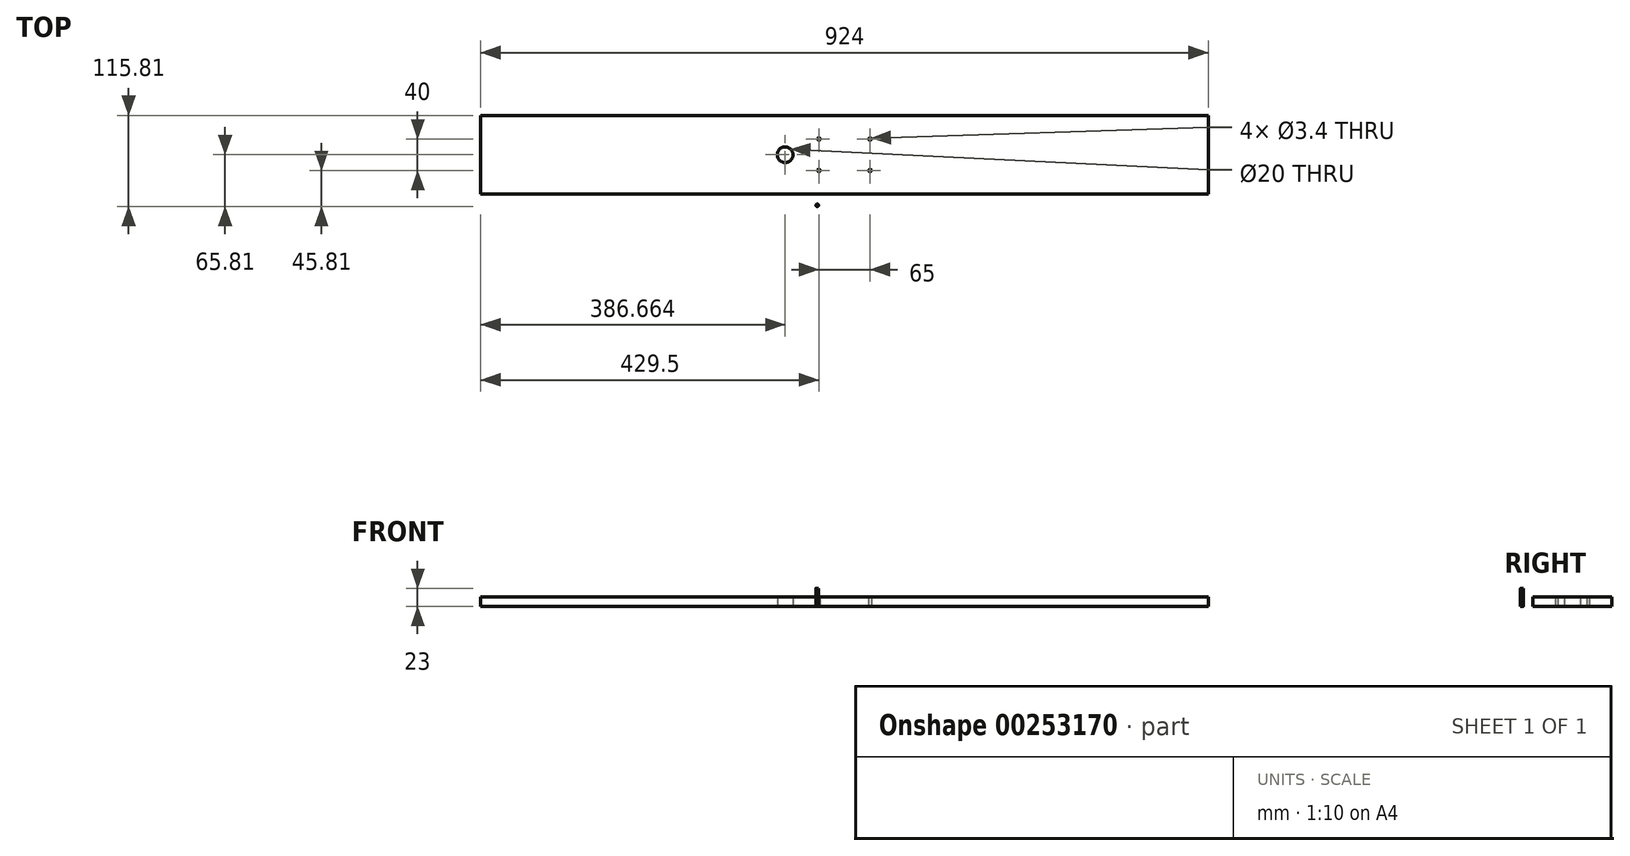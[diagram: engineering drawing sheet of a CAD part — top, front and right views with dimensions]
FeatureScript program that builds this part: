
annotation { "Feature Type Name" : "Feature", "Feature Type Description" : "" }
export const myFeature = defineFeature(function(context is Context, id is Id, definition is map)
    precondition{}
    {
        {
            var Q0;
            Q0=qCreatedBy(makeId("Top.planeOp"),FACE);
            var sketch = newSketch(context, id + "F0", { "sketchPlane" : qUnion([Q0])});
            skLineSegment(sketch, "E0.bottom", {"start": v(-462, 50) * mm, "end": v(462, 50) * mm});
            skLineSegment(sketch, "E0.top", {"start": v(-462, -50) * mm, "end": v(462, -50) * mm});
            skLineSegment(sketch, "E0.left", {"start": v(-462, 50) * mm, "end": v(-462, -50) * mm});
            skLineSegment(sketch, "E0.right", {"start": v(462, 50) * mm, "end": v(462, -50) * mm});
            skSolve(sketch);
        }
        {
            var Q0;
            Q0 = qSketchRegion(id + "F0", true);
            extrude(context, id + "F1", {"entities" : qUnion([Q0]), "depth" : 12 * mm});
        }
        {
            var Q0;
            Q0=makeQuery(id+"F1.opExtrude","CAP_FACE",FACE,{"disambiguationData":[OSD([sQuery(id+"F0.wireOp",EDGE,"E0.bottom"),sQuery(id+"F0.wireOp",EDGE,"E0.top"),sQuery(id+"F0.wireOp",EDGE,"E0.left"),sQuery(id+"F0.wireOp",EDGE,"E0.right")])],"isStart":true});
            var sketch = newSketch(context, id + "F2", { "sketchPlane" : qUnion([Q0])});
            skLineSegment(sketch, "E1.bottom", {"start": v(-32.5, 20) * mm, "end": v(32.5, 20) * mm, "construction": true});
            skLineSegment(sketch, "E1.top", {"start": v(-32.5, -20) * mm, "end": v(32.5, -20) * mm, "construction": true});
            skLineSegment(sketch, "E1.left", {"start": v(-32.5, 20) * mm, "end": v(-32.5, -20) * mm, "construction": true});
            skLineSegment(sketch, "E1.right", {"start": v(32.5, 20) * mm, "end": v(32.5, -20) * mm, "construction": true});
            skCircle(sketch, "E2", {"center": v(-32.5, 20) * mm, "radius": 1.7 * mm});
            skCircle(sketch, "E3", {"center": v(32.5, 20) * mm, "radius": 1.7 * mm});
            skCircle(sketch, "E4", {"center": v(32.5, -20) * mm, "radius": 1.7 * mm});
            skCircle(sketch, "E5", {"center": v(-32.5, -20) * mm, "radius": 1.7 * mm});
            skCircle(sketch, "E6", {"center": v(-75.34, 0) * mm, "radius": 10 * mm});
            skSolve(sketch);
        }
        {
            var Q0;
            Q0=makeQuery(id+"F2.imprint","IMPRINT",FACE,{"disambiguationData":[TD([[makeQuery(id+"F2.imprint","IMPRINT",EDGE,{"derivedFrom":sQuery(id+"F2.wireOp",EDGE,"E6")}),1.0]])]});
            extrude(context, id + "F3", {"entities" : qUnion([Q0]), "operationType" : NewBodyOperationType.REMOVE, "oppositeDirection" : true, "depth" : 25 * mm});
        }
        {
            var Q0;
            Q0=makeQuery(id+"F2.imprint","IMPRINT",FACE,{"disambiguationData":[TD([[makeQuery(id+"F2.imprint","IMPRINT",EDGE,{"derivedFrom":sQuery(id+"F2.wireOp",EDGE,"E4")}),1.0]])]});
            var Q1;
            Q1=makeQuery(id+"F2.imprint","IMPRINT",FACE,{"disambiguationData":[TD([[makeQuery(id+"F2.imprint","IMPRINT",EDGE,{"derivedFrom":sQuery(id+"F2.wireOp",EDGE,"E5")}),1.0]])]});
            var Q2;
            Q2=makeQuery(id+"F2.imprint","IMPRINT",FACE,{"disambiguationData":[TD([[makeQuery(id+"F2.imprint","IMPRINT",EDGE,{"derivedFrom":sQuery(id+"F2.wireOp",EDGE,"E3")}),1.0]])]});
            var Q3;
            Q3=makeQuery(id+"F2.imprint","IMPRINT",FACE,{"disambiguationData":[TD([[makeQuery(id+"F2.imprint","IMPRINT",EDGE,{"derivedFrom":sQuery(id+"F2.wireOp",EDGE,"E2")}),1.0]])]});
            extrude(context, id + "F4", {"entities" : qUnion([Q0, Q1, Q2, Q3]), "operationType" : NewBodyOperationType.REMOVE, "oppositeDirection" : true, "depth" : 25 * mm});
        }
        {
            var Q0;
            Q0=qCreatedBy(makeId("Top.planeOp"),FACE);
            var sketch = newSketch(context, id + "F5", { "sketchPlane" : qUnion([Q0])});
            skCircle(sketch, "E7", {"center": v(-34.73, -64.11) * mm, "radius": 1.7 * mm});
            skSolve(sketch);
        }
        {
            var Q0;
            Q0=makeQuery(id+"F5.imprint","IMPRINT",FACE,{"disambiguationData":[TD([[makeQuery(id+"F5.imprint","IMPRINT",EDGE,{"derivedFrom":sQuery(id+"F5.wireOp",EDGE,"E7")}),1.0]])]});
            extrude(context, id + "F6", {"entities" : qUnion([Q0]), "depth" : 23 * mm});
        }
    });
